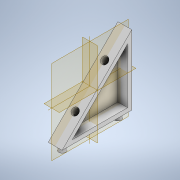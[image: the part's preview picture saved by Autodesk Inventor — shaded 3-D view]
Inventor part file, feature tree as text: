
AUTODESK INVENTOR PART (.ipt)
format: ipt  version: 2022.4 (Build 264492010, 492A)  size: 141,312 bytes
history: native  units: mm
features: extrude x4, sketch x4
ambient origin geometry x8: Origin, YZ Plane, XZ Plane, XY Plane, X Axis, Y Axis, Z Axis, Center Point
bodies: Solid1 (feature_tree)
feature tree (8):
  extrude  "Extrusion1"  Depth=50.0mm
  extrude  "Extrusion2"  Depth=3.0mm
  extrude  "Extrusion3"  Depth=5.0mm
  extrude  "Extrusion4"  Depth=10.0mm
  sketch  "Sketch2"  dims[d0=50.0mm d1=50.0mm]
  sketch  "Sketch4"  dims[d2=10.0mm d3=0.0mm d8=3.0mm]
  sketch  "Sketch5"  dims[d9=7.0mm d10=0.0mm d11=5.0mm]
  sketch  "Sketch8"  dims[d12=5.0mm d13=20.0mm d15=40.0mm d16=10.0mm d18=10.0mm d20=5.0mm d21=0.0mm d31=70.710678mm d32=5.0mm d34=15.0mm d35=7.0mm d36=0.0mm]
